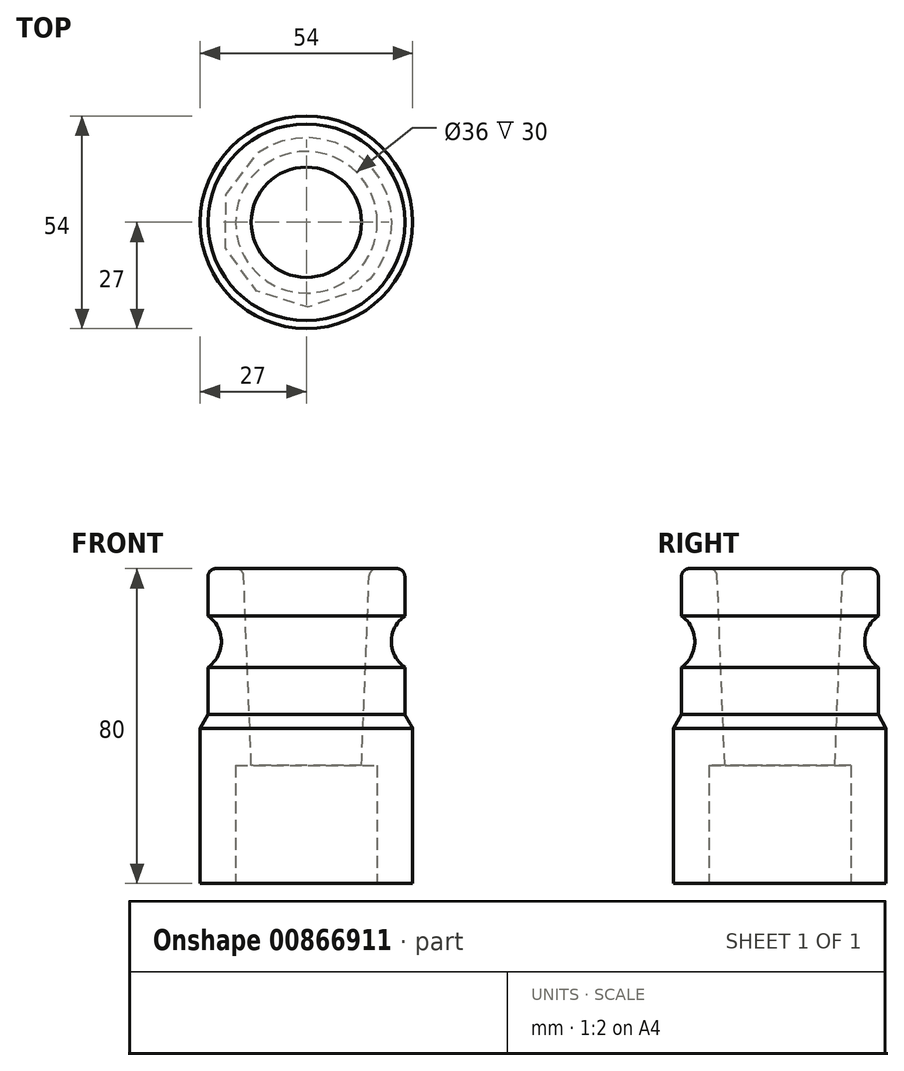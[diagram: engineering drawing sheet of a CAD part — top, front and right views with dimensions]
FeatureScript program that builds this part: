
annotation { "Feature Type Name" : "Feature", "Feature Type Description" : "" }
export const myFeature = defineFeature(function(context is Context, id is Id, definition is map)
    precondition{}
    {
        {
            var Q0;
            Q0=qCreatedBy(makeId("Front.planeOp"),FACE);
            var sketch = newSketch(context, id + "F0", { "sketchPlane" : qUnion([Q0])});
            skLineSegment(sketch, "E0", {"start": v(-16, 40.56) * mm, "end": v(-25, 40.56) * mm});
            skLineSegment(sketch, "E1", {"start": v(-18, -39.44) * mm, "end": v(-14, -39.44) * mm});
            skLineSegment(sketch, "E2", {"start": v(-27, -39.44) * mm, "end": v(-18, -39.44) * mm});
            skLineSegment(sketch, "E3", {"start": v(-16, 40.56) * mm, "end": v(-14, -9.44) * mm});
            skLineSegment(sketch, "E4", {"start": v(-14, -9.44) * mm, "end": v(-14, -39.44) * mm});
            skLineSegment(sketch, "E5", {"start": v(0, 51.78) * mm, "end": v(0, -55.23) * mm, "construction": true});
            skLineSegment(sketch, "E6", {"start": v(-25, 40.56) * mm, "end": v(-25, 28.56) * mm});
            skArc(sketch, "E7", {"start": v(-25, 15.46) * mm, "mid": v(-21.6, 22.01) * mm, "end": v(-25, 28.56) * mm});
            skLineSegment(sketch, "E8", {"start": v(-27, 0) * mm, "end": v(-27, -39.44) * mm});
            skLineSegment(sketch, "E9", {"start": v(-25, 15.46) * mm, "end": v(-25, 3.46) * mm});
            skLineSegment(sketch, "E10", {"start": v(-25, 3.46) * mm, "end": v(-27, 0) * mm});
            skLineSegment(sketch, "E11", {"start": v(-62.5, 0) * mm, "end": v(59.39, 0) * mm, "construction": true});
            skSolve(sketch);
        }
        {
            var Q0;
            Q0=makeQuery(id+"F0.imprint","IMPRINT",FACE,{"disambiguationData":[TD([[makeQuery(id+"F0.imprint","IMPRINT",EDGE,{"derivedFrom":sQuery(id+"F0.wireOp",EDGE,"E0")}),1.0]])]});
            var Q1;
            {var subQ0=sQuery(id+"F0.wireOp",EDGE,"1vsp6pBn-idtG-G3rb-hdMj-pUcK1OkQxKzT");Q1=makeQuery(id+"F0.imprint","IMPRINT",FACE,{"disambiguationData":[TD([[makeQuery(id+"F0.imprint","IMPRINT",EDGE,{"derivedFrom":subQ0}),-1.0]])]});}
            var Q2;
            Q2=sQuery(id+"F0.wireOp",EDGE,"E5");
            revolve(context, id + "F1", {"surfaceOperationType" : NewSurfaceOperationType.NEW, "entities" : qUnion([Q0, Q1]), "axis" : qUnion([Q2]), "revolveType" : RevolveType.FULL});
        }
        {
            var Q0;
            Q0=makeQuery(id+"F1.opRevolve","SWEPT_EDGE",EDGE,{"disambiguationData":[OSD([sQuery(id+"F0.wireOp",EDGE,"E0"),sQuery(id+"F0.wireOp",EDGE,"QTyNFRFm-ZTnk-eFEA-kTw0-o0j1b9QocP6I")])]});
            fillet(context, id + "F2", {"entities" : qUnion([Q0]), "radius" : 2 * mm, "tangentPropagation" : true, "allowEdgeOverflow" : false});
        }
        {
            var Q0;
            Q0=makeQuery(id+"F1.opRevolve","SWEPT_FACE",FACE,{"disambiguationData":[OSD([sQuery(id+"F0.wireOp",EDGE,"E1"),sQuery(id+"F0.wireOp",EDGE,"E2")])]});
            var sketch = newSketch(context, id + "F3", { "sketchPlane" : qUnion([Q0])});
            skCircle(sketch, "E12", {"center": v(0, 0) * mm, "radius": 18 * mm});
            skSolve(sketch);
        }
        {
            var Q0;
            Q0=makeQuery(id+"F3.imprint","IMPRINT",FACE,{"disambiguationData":[TD([[makeQuery(id+"F3.imprint","IMPRINT",EDGE,{"derivedFrom":sQuery(id+"F3.wireOp",EDGE,"E12")}),1.0]])]});
            extrude(context, id + "F4", {"entities" : qUnion([Q0]), "operationType" : NewBodyOperationType.REMOVE, "oppositeDirection" : true, "depth" : 30 * mm, "offsetDistance" : 25 * mm});
        }
    });
